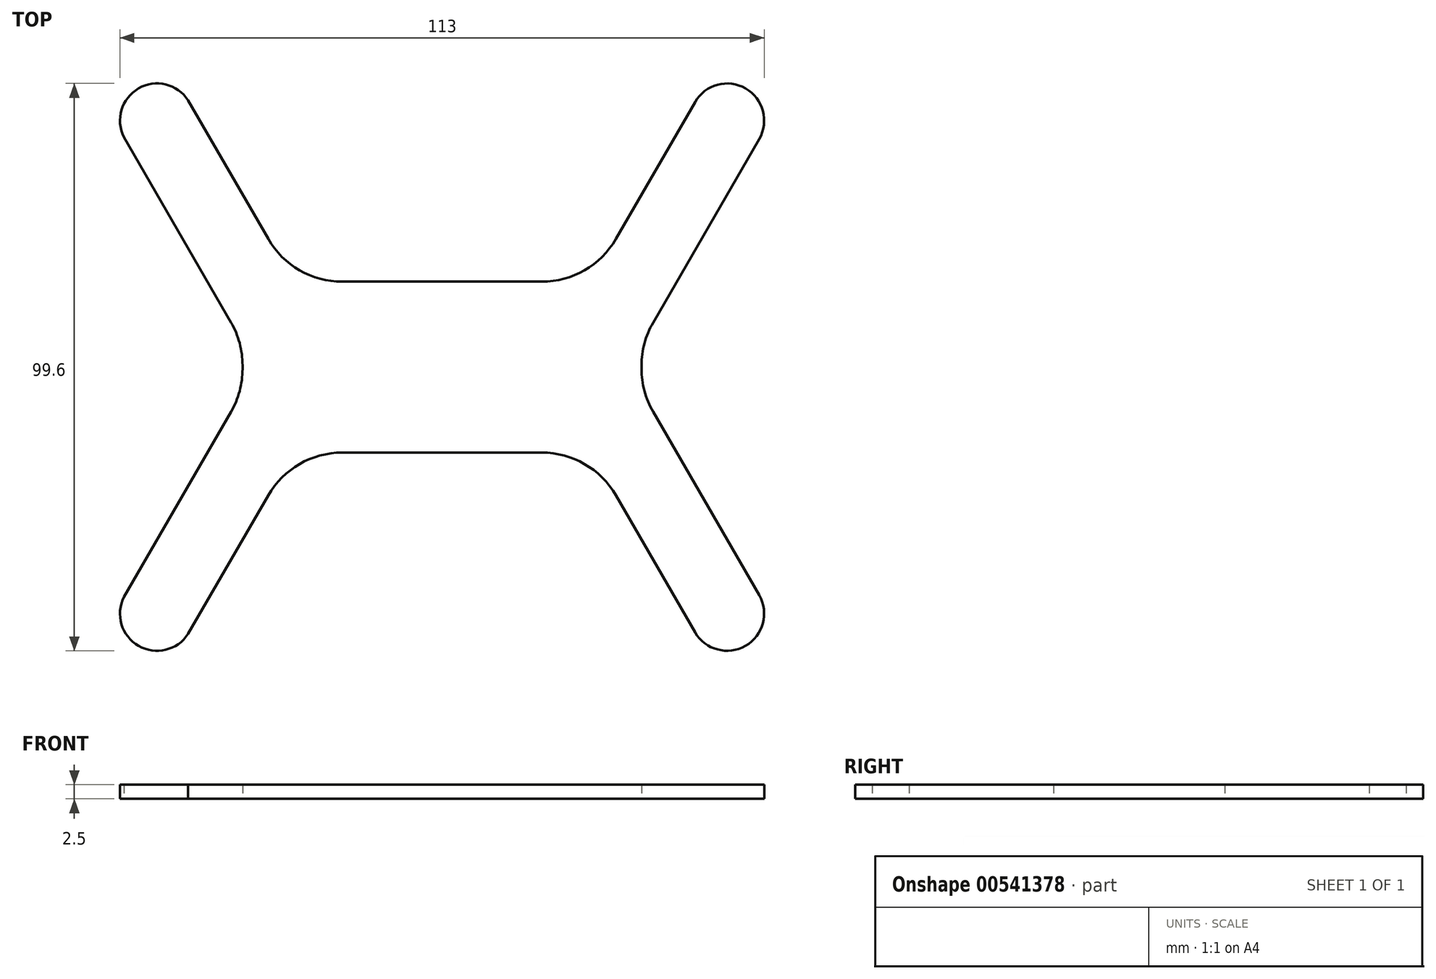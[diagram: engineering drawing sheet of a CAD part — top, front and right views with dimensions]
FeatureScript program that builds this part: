
annotation { "Feature Type Name" : "Feature", "Feature Type Description" : "" }
export const myFeature = defineFeature(function(context is Context, id is Id, definition is map)
    precondition{}
    {
        {
            var Q0;
            Q0=qCreatedBy(makeId("Top.planeOp"),FACE);
            var sketch = newSketch(context, id + "F0", { "sketchPlane" : qUnion([Q0])});
            skCircle(sketch, "E0", {"center": v(-50, 43.3) * mm, "radius": 6.5 * mm, "construction": true});
            skCircle(sketch, "E1", {"center": v(-50, -43.3) * mm, "radius": 6.5 * mm, "construction": true});
            skCircle(sketch, "E2", {"center": v(50, 43.3) * mm, "radius": 6.5 * mm, "construction": true});
            skCircle(sketch, "E3", {"center": v(50, -43.3) * mm, "radius": 6.5 * mm, "construction": true});
            skLineSegment(sketch, "E4", {"start": v(-50, 43.3) * mm, "end": v(-25, 0) * mm, "construction": true});
            skLineSegment(sketch, "E5", {"start": v(-25, 0) * mm, "end": v(-50, -43.3) * mm, "construction": true});
            skLineSegment(sketch, "E6", {"start": v(50, 43.3) * mm, "end": v(25, 0) * mm, "construction": true});
            skLineSegment(sketch, "E7", {"start": v(25, 0) * mm, "end": v(50, -43.3) * mm, "construction": true});
            skLineSegment(sketch, "E8.bottom", {"start": v(-35, 15) * mm, "end": v(35, 15) * mm, "construction": true});
            skLineSegment(sketch, "E8.top", {"start": v(-35, -15) * mm, "end": v(35, -15) * mm, "construction": true});
            skLineSegment(sketch, "E8.left", {"start": v(-35, 15) * mm, "end": v(-35, -15) * mm, "construction": true});
            skLineSegment(sketch, "E8.right", {"start": v(35, 15) * mm, "end": v(35, -15) * mm, "construction": true});
            skLineSegment(sketch, "E9", {"start": v(-55.8, 40.35) * mm, "end": v(-35, 4.34) * mm});
            skLineSegment(sketch, "E10", {"start": v(-55.8, 40.35) * mm, "end": v(-44.55, 46.84) * mm, "construction": true});
            skLineSegment(sketch, "E11", {"start": v(-44.55, 46.84) * mm, "end": v(-26.16, 15) * mm});
            skArc(sketch, "E12", {"start": v(-44.55, 46.84) * mm, "mid": v(-53.25, 48.93) * mm, "end": v(-55.8, 40.35) * mm});
            skLineSegment(sketch, "E13", {"start": v(-26.16, 15) * mm, "end": v(0, 15) * mm});
            skLineSegment(sketch, "E14", {"start": v(-35, 4.34) * mm, "end": v(-35, 0) * mm});
            skLineSegment(sketch, "E15", {"start": v(44.37, 46.55) * mm, "end": v(26.15, 15) * mm});
            skLineSegment(sketch, "E16", {"start": v(55.63, 40.05) * mm, "end": v(35, 4.32) * mm});
            skLineSegment(sketch, "E17", {"start": v(50, 43.3) * mm, "end": v(55.63, 40.05) * mm, "construction": true});
            skLineSegment(sketch, "E18", {"start": v(50, 43.3) * mm, "end": v(44.37, 46.55) * mm, "construction": true});
            skArc(sketch, "E19", {"start": v(55.63, 40.05) * mm, "mid": v(53.25, 48.93) * mm, "end": v(44.37, 46.55) * mm});
            skLineSegment(sketch, "E20", {"start": v(26.15, 15) * mm, "end": v(0, 15) * mm});
            skLineSegment(sketch, "E21", {"start": v(35, 4.32) * mm, "end": v(35, 0) * mm});
            skLineSegment(sketch, "E22.MirrorCS", {"start": v(-26.16, -15) * mm, "end": v(0, -15) * mm});
            skArc(sketch, "E23.MirrorCS", {"start": v(55.63, -40.05) * mm, "mid": v(53.25, -48.93) * mm, "end": v(44.37, -46.55) * mm});
            skLineSegment(sketch, "E24.MirrorCS", {"start": v(26.15, -15) * mm, "end": v(0, -15) * mm});
            skArc(sketch, "E25.MirrorCS", {"start": v(-44.55, -46.84) * mm, "mid": v(-53.25, -48.93) * mm, "end": v(-55.8, -40.35) * mm});
            skLineSegment(sketch, "E26.MirrorCS", {"start": v(44.37, -46.55) * mm, "end": v(26.15, -15) * mm});
            skLineSegment(sketch, "E27.MirrorCS", {"start": v(-44.55, -46.84) * mm, "end": v(-26.16, -15) * mm});
            skLineSegment(sketch, "E28.MirrorCS", {"start": v(-35, -4.34) * mm, "end": v(-35, 0) * mm});
            skLineSegment(sketch, "E29.MirrorCS", {"start": v(-55.8, -40.35) * mm, "end": v(-44.55, -46.84) * mm, "construction": true});
            skLineSegment(sketch, "E30.MirrorCS", {"start": v(50, -43.3) * mm, "end": v(55.63, -40.05) * mm, "construction": true});
            skLineSegment(sketch, "E31.MirrorCS", {"start": v(55.63, -40.05) * mm, "end": v(35, -4.32) * mm});
            skLineSegment(sketch, "E32.MirrorCS", {"start": v(-55.8, -40.35) * mm, "end": v(-35, -4.34) * mm});
            skLineSegment(sketch, "E33.MirrorCS", {"start": v(50, -43.3) * mm, "end": v(44.37, -46.55) * mm, "construction": true});
            skLineSegment(sketch, "E34.MirrorCS", {"start": v(-50, -43.3) * mm, "end": v(-25, 0) * mm, "construction": true});
            skLineSegment(sketch, "E35.MirrorCS", {"start": v(50, -43.3) * mm, "end": v(25, 0) * mm, "construction": true});
            skLineSegment(sketch, "E36.MirrorCS", {"start": v(35, -4.32) * mm, "end": v(35, 0) * mm});
            skSolve(sketch);
        }
        {
            var Q0;
            Q0=makeQuery(id+"F0.imprint","IMPRINT",FACE,{"disambiguationData":[TD([[makeQuery(id+"F0.imprint","IMPRINT",EDGE,{"derivedFrom":sQuery(id+"F0.wireOp",EDGE,"E9")}),1.0]])]});
            extrude(context, id + "F1", {"entities" : qUnion([Q0]), "depth" : 2.5 * mm, "offsetDistance" : 25 * mm});
        }
        {
            var Q0;
            Q0=makeQuery(id+"F1.opExtrude","SWEPT_EDGE",EDGE,{"disambiguationData":[OSD([sQuery(id+"F0.wireOp",EDGE,"E15"),sQuery(id+"F0.wireOp",EDGE,"E20")])]});
            var Q1;
            Q1=makeQuery(id+"F1.opExtrude","SWEPT_EDGE",EDGE,{"disambiguationData":[OSD([sQuery(id+"F0.wireOp",EDGE,"E11"),sQuery(id+"F0.wireOp",EDGE,"E13")])]});
            var Q2;
            Q2=makeQuery(id+"F1.opExtrude","SWEPT_EDGE",EDGE,{"disambiguationData":[OSD([sQuery(id+"F0.wireOp",EDGE,"E24.MirrorCS"),sQuery(id+"F0.wireOp",EDGE,"E26.MirrorCS")])]});
            var Q3;
            Q3=makeQuery(id+"F1.opExtrude","SWEPT_EDGE",EDGE,{"disambiguationData":[OSD([sQuery(id+"F0.wireOp",EDGE,"E22.MirrorCS"),sQuery(id+"F0.wireOp",EDGE,"E27.MirrorCS")])]});
            var Q4;
            Q4=makeQuery(id+"F1.opExtrude","SWEPT_EDGE",EDGE,{"disambiguationData":[OSD([sQuery(id+"F0.wireOp",EDGE,"E28.MirrorCS"),sQuery(id+"F0.wireOp",EDGE,"E32.MirrorCS")])]});
            var Q5;
            Q5=makeQuery(id+"F1.opExtrude","SWEPT_EDGE",EDGE,{"disambiguationData":[OSD([sQuery(id+"F0.wireOp",EDGE,"E9"),sQuery(id+"F0.wireOp",EDGE,"E14")])]});
            var Q6;
            Q6=makeQuery(id+"F1.opExtrude","SWEPT_EDGE",EDGE,{"disambiguationData":[OSD([sQuery(id+"F0.wireOp",EDGE,"E31.MirrorCS"),sQuery(id+"F0.wireOp",EDGE,"E36.MirrorCS")])]});
            var Q7;
            Q7=makeQuery(id+"F1.opExtrude","SWEPT_EDGE",EDGE,{"disambiguationData":[OSD([sQuery(id+"F0.wireOp",EDGE,"E16"),sQuery(id+"F0.wireOp",EDGE,"E21")])]});
            fillet(context, id + "F2", {"entities" : qUnion([Q0, Q1, Q2, Q3, Q4, Q5, Q6, Q7]), "radius" : 15 * mm, "tangentPropagation" : true, "allowEdgeOverflow" : false});
        }
    });
